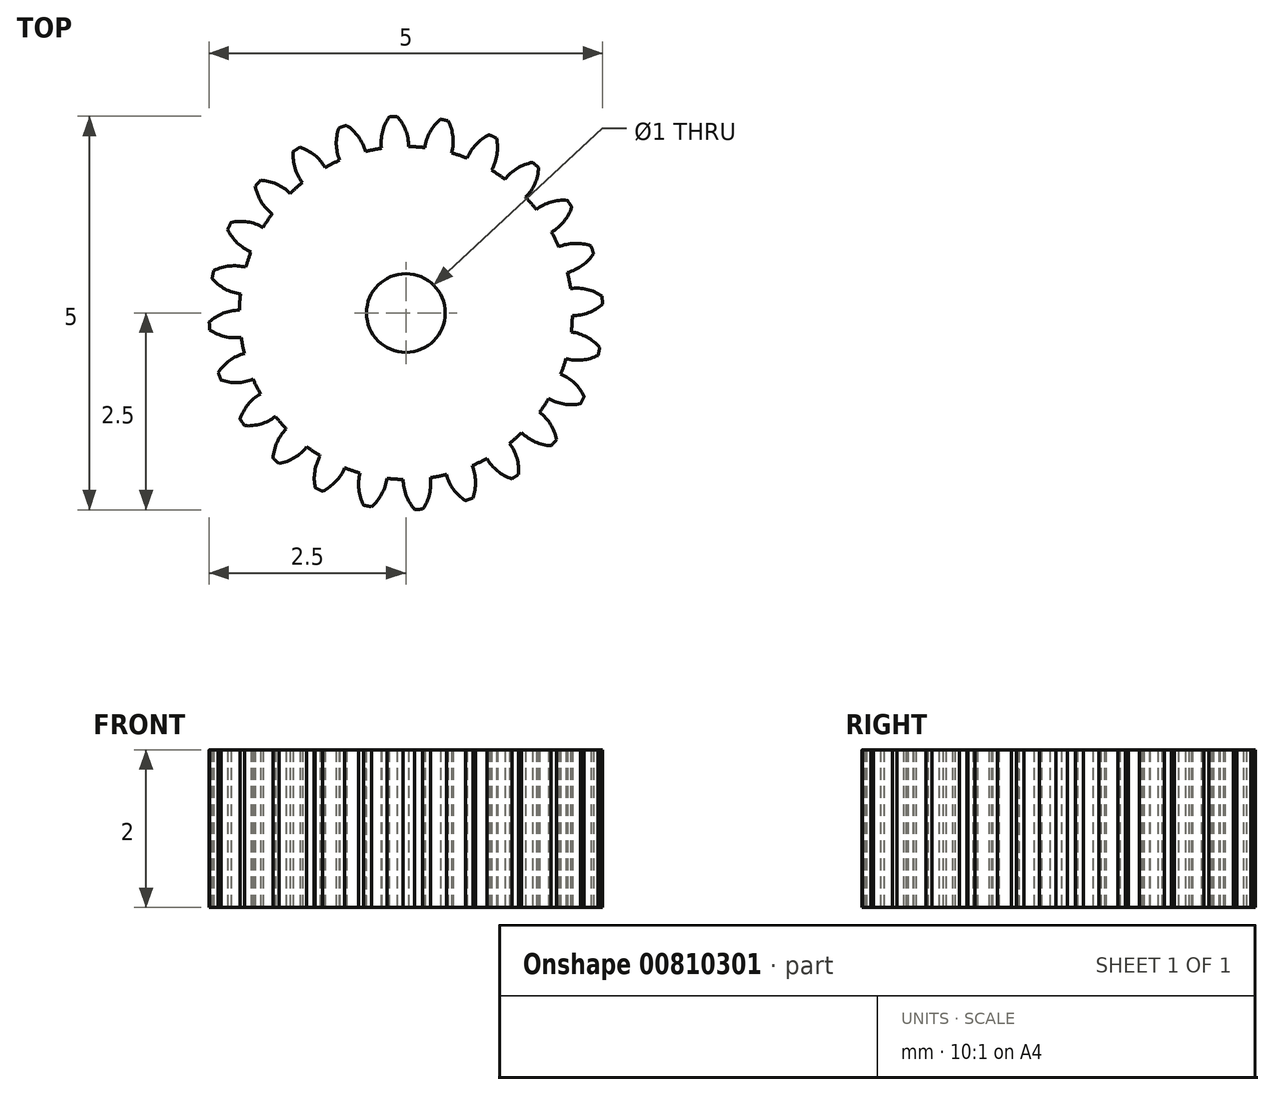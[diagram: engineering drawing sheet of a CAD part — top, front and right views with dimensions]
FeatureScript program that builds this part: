
annotation { "Feature Type Name" : "Feature", "Feature Type Description" : "" }
export const myFeature = defineFeature(function(context is Context, id is Id, definition is map)
    precondition{}
    {
        {
            var Q0;
            Q0=qCreatedBy(makeId("Top.planeOp"),FACE);
            var sketch = newSketch(context, id + "F0", { "sketchPlane" : qUnion([Q0])});
            skCircle(sketch, "E0", {"center": v(0, 0) * mm, "radius": 2.5 * mm, "construction": true});
            skCircle(sketch, "E1", {"center": v(0, 0) * mm, "radius": 2.31 * mm, "construction": true});
            skCircle(sketch, "E2", {"center": v(0, 0) * mm, "radius": 2.12 * mm});
            skLineSegment(sketch, "E3", {"start": v(0, 0) * mm, "end": v(0, 5.24) * mm, "construction": true});
            skLineSegment(sketch, "E4", {"start": v(0, 0) * mm, "end": v(-0.2, 3) * mm, "construction": true});
            skLineSegment(sketch, "E5", {"start": v(0, 2.31) * mm, "end": v(-3.07, 2.31) * mm, "construction": true});
            skLineSegment(sketch, "E6", {"start": v(0, 2.31) * mm, "end": v(-2.95, 1.24) * mm, "construction": true});
            skCircle(sketch, "E7", {"center": v(0, 2.31) * mm, "radius": 0.57 * mm, "construction": true});
            skCircle(sketch, "E8", {"center": v(0, 0) * mm, "radius": 2.17 * mm, "construction": true});
            skCircle(sketch, "E9", {"center": v(-0.54, 2.11) * mm, "radius": 0.57 * mm, "construction": true});
            skArc(sketch, "E10", {"start": v(0, 2.31) * mm, "mid": v(-0.05, 2.4) * mm, "end": v(-0.11, 2.5) * mm});
            skArc(sketch, "E11", {"start": v(0.03, 2.11) * mm, "mid": v(0.03, 2.21) * mm, "end": v(0, 2.31) * mm});
            skArc(sketch, "E12.MirrorCS", {"start": v(-0.3, 2.3) * mm, "mid": v(-0.27, 2.4) * mm, "end": v(-0.21, 2.5) * mm});
            skArc(sketch, "E13.MirrorCS", {"start": v(-0.31, 2.1) * mm, "mid": v(-0.31, 2.2) * mm, "end": v(-0.3, 2.3) * mm});
            skArc(sketch, "E14", {"start": v(-0.11, 2.5) * mm, "mid": v(-0.16, 2.5) * mm, "end": v(-0.21, 2.5) * mm});
            skSolve(sketch);
        }
        {
            var Q0;
            Q0 = qSketchRegion(id + "F0", true);
            extrude(context, id + "F1", {"entities" : qUnion([Q0]), "depth" : 2 * mm, "offsetDistance" : 25 * mm});
        }
        {
            var Q0;
            Q0=makeQuery(id+"F1.opExtrude","SWEPT_BODY",BODY,{"disambiguationData":[OSD([sQuery(id+"F0.wireOp",EDGE,"E2"),sQuery(id+"F0.wireOp",EDGE,"E10"),sQuery(id+"F0.wireOp",EDGE,"E11"),sQuery(id+"F0.wireOp",EDGE,"E12.MirrorCS"),sQuery(id+"F0.wireOp",EDGE,"E13.MirrorCS"),sQuery(id+"F0.wireOp",EDGE,"E14")])]});
            var Q1;
            Q1=makeQuery(id+"F1.opExtrude","SWEPT_FACE",FACE,{"disambiguationData":[OSD([sQuery(id+"F0.wireOp",EDGE,"E2")])]});
            circularPattern(context, id + "F2", {"operationType" : NewBodyOperationType.ADD, "entities" : qUnion([Q0]), "axis" : qUnion([Q1]), "angle" : 360 * degree, "instanceCount" : 24, "equalSpace" : true});
        }
        {
            var Q0;
            {var subQ0=makeQuery(id+"F1.opExtrude","CAP_FACE",FACE,{"disambiguationData":[OSD([sQuery(id+"F0.wireOp",EDGE,"E2"),sQuery(id+"F0.wireOp",EDGE,"E10"),sQuery(id+"F0.wireOp",EDGE,"E11"),sQuery(id+"F0.wireOp",EDGE,"E12.MirrorCS"),sQuery(id+"F0.wireOp",EDGE,"E13.MirrorCS"),sQuery(id+"F0.wireOp",EDGE,"E14")])],"isStart":false});Q0=makeQuery(id+"F2.boolean.opBoolean","MERGE",FACE,{"derivedFrom":[subQ0,makeQuery(id+"F2.opPattern","COPY",FACE,{"derivedFrom":subQ0,"instanceName":"1"}),makeQuery(id+"F2.opPattern","COPY",FACE,{"derivedFrom":subQ0,"instanceName":"2"}),makeQuery(id+"F2.opPattern","COPY",FACE,{"derivedFrom":subQ0,"instanceName":"3"}),makeQuery(id+"F2.opPattern","COPY",FACE,{"derivedFrom":subQ0,"instanceName":"4"}),makeQuery(id+"F2.opPattern","COPY",FACE,{"derivedFrom":subQ0,"instanceName":"5"}),makeQuery(id+"F2.opPattern","COPY",FACE,{"derivedFrom":subQ0,"instanceName":"6"}),makeQuery(id+"F2.opPattern","COPY",FACE,{"derivedFrom":subQ0,"instanceName":"7"}),makeQuery(id+"F2.opPattern","COPY",FACE,{"derivedFrom":subQ0,"instanceName":"8"}),makeQuery(id+"F2.opPattern","COPY",FACE,{"derivedFrom":subQ0,"instanceName":"9"}),makeQuery(id+"F2.opPattern","COPY",FACE,{"derivedFrom":subQ0,"instanceName":"10"}),makeQuery(id+"F2.opPattern","COPY",FACE,{"derivedFrom":subQ0,"instanceName":"11"}),makeQuery(id+"F2.opPattern","COPY",FACE,{"derivedFrom":subQ0,"instanceName":"12"}),makeQuery(id+"F2.opPattern","COPY",FACE,{"derivedFrom":subQ0,"instanceName":"13"}),makeQuery(id+"F2.opPattern","COPY",FACE,{"derivedFrom":subQ0,"instanceName":"14"}),makeQuery(id+"F2.opPattern","COPY",FACE,{"derivedFrom":subQ0,"instanceName":"15"}),makeQuery(id+"F2.opPattern","COPY",FACE,{"derivedFrom":subQ0,"instanceName":"16"}),makeQuery(id+"F2.opPattern","COPY",FACE,{"derivedFrom":subQ0,"instanceName":"17"}),makeQuery(id+"F2.opPattern","COPY",FACE,{"derivedFrom":subQ0,"instanceName":"18"}),makeQuery(id+"F2.opPattern","COPY",FACE,{"derivedFrom":subQ0,"instanceName":"19"}),makeQuery(id+"F2.opPattern","COPY",FACE,{"derivedFrom":subQ0,"instanceName":"20"}),makeQuery(id+"F2.opPattern","COPY",FACE,{"derivedFrom":subQ0,"instanceName":"21"}),makeQuery(id+"F2.opPattern","COPY",FACE,{"derivedFrom":subQ0,"instanceName":"22"}),makeQuery(id+"F2.opPattern","COPY",FACE,{"derivedFrom":subQ0,"instanceName":"23"})]});}
            var sketch = newSketch(context, id + "F3", { "sketchPlane" : qUnion([Q0])});
            skCircle(sketch, "E15", {"center": v(0, 0) * mm, "radius": 0.5 * mm});
            skSolve(sketch);
        }
        {
            var Q0;
            Q0=makeQuery(id+"F3.imprint","IMPRINT",FACE,{"disambiguationData":[TD([[makeQuery(id+"F3.imprint","IMPRINT",EDGE,{"derivedFrom":sQuery(id+"F3.wireOp",EDGE,"E15")}),1.0]])]});
            extrude(context, id + "F4", {"entities" : qUnion([Q0]), "operationType" : NewBodyOperationType.REMOVE, "endBound" : BoundingType.THROUGH_ALL, "oppositeDirection" : true, "depth" : 25 * mm, "offsetDistance" : 25 * mm});
        }
    });
